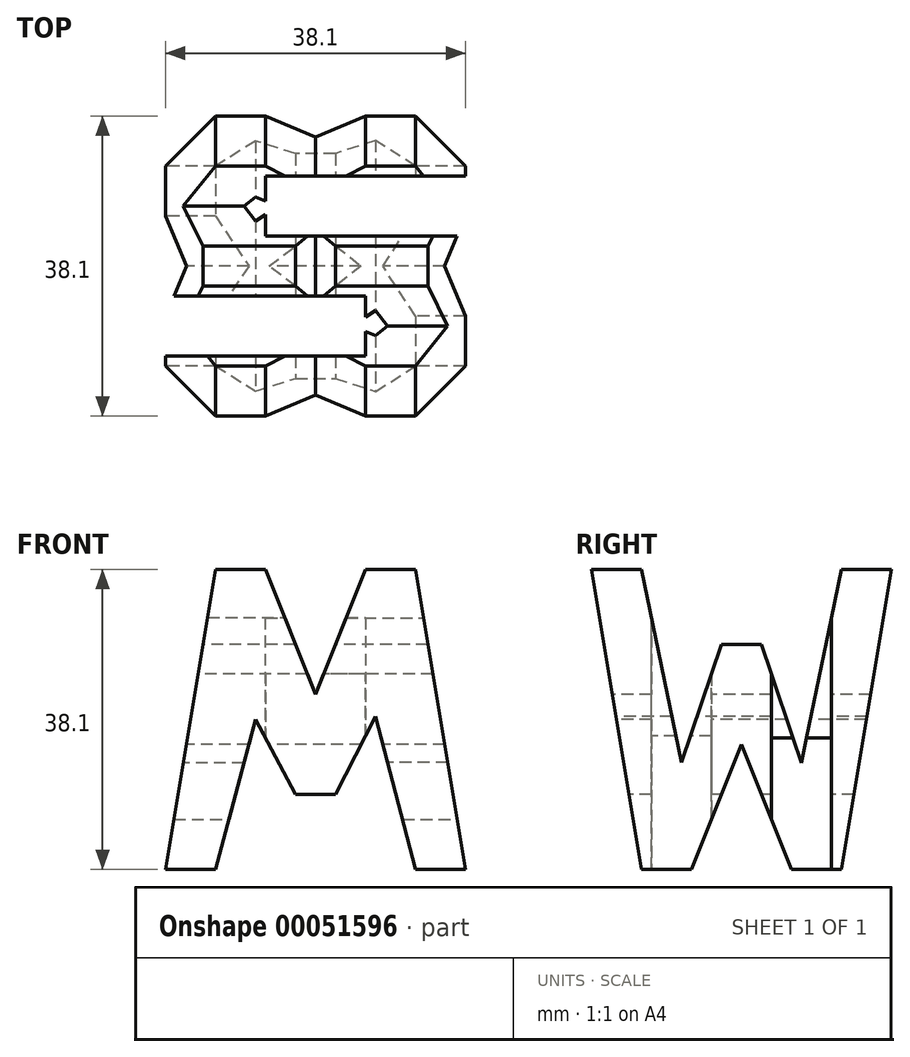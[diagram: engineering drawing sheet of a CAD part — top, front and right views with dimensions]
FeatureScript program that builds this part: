
annotation { "Feature Type Name" : "Feature", "Feature Type Description" : "" }
export const myFeature = defineFeature(function(context is Context, id is Id, definition is map)
    precondition{}
    {
        {
            var Q0;
            Q0=qCreatedBy(makeId("Front.planeOp"),FACE);
            var sketch = newSketch(context, id + "F0", { "sketchPlane" : qUnion([Q0])});
            skLineSegment(sketch, "E0", {"start": v(0, 0) * mm, "end": v(-38.1, 0) * mm});
            skLineSegment(sketch, "E1", {"start": v(-38.1, 0) * mm, "end": v(-38.1, 38.1) * mm});
            skLineSegment(sketch, "E2", {"start": v(-38.1, 38.1) * mm, "end": v(0, 38.1) * mm});
            skLineSegment(sketch, "E3", {"start": v(0, 38.1) * mm, "end": v(0, 0) * mm});
            skSolve(sketch);
        }
        {
            var Q0;
            Q0=makeQuery(id+"F0.imprint","IMPRINT",FACE,{"disambiguationData":[TD([[makeQuery(id+"F0.imprint","IMPRINT",EDGE,{"derivedFrom":sQuery(id+"F0.wireOp",EDGE,"E0")}),-1.0]])]});
            extrude(context, id + "F1", {"entities" : qUnion([Q0]), "depth" : 38.1 * mm});
        }
        {
            var Q0;
            Q0=qCreatedBy(makeId("Front.planeOp"),FACE);
            cPlane(context, id + "F2", {"entities" : qUnion([Q0]), "cplaneType" : CPlaneType.OFFSET, "offset" : 38.1 * mm, "width" : 152.4 * mm, "height" : 152.4 * mm});
        }
        {
            var Q0;
            Q0=qCreatedBy(makeId("Right.planeOp"),FACE);
            cPlane(context, id + "F3", {"entities" : qUnion([Q0]), "cplaneType" : CPlaneType.OFFSET, "offset" : 38.1 * mm, "oppositeDirection" : true, "width" : 152.4 * mm, "height" : 152.4 * mm});
        }
        {
            var Q0;
            Q0=qCreatedBy(makeId("Top.planeOp"),FACE);
            cPlane(context, id + "F4", {"entities" : qUnion([Q0]), "cplaneType" : CPlaneType.OFFSET, "offset" : 38.1 * mm, "width" : 152.4 * mm, "height" : 152.4 * mm});
        }
        {
            var Q0;
            Q0=qCreatedBy(id+"F3.planeOp",FACE);
            var sketch = newSketch(context, id + "F5", { "sketchPlane" : qUnion([Q0])});
            skLineSegment(sketch, "E4", {"start": v(0, 0) * mm, "end": v(0, 38.1) * mm});
            skLineSegment(sketch, "E5", {"start": v(0, 38.1) * mm, "end": v(-38.1, 38.1) * mm});
            skLineSegment(sketch, "E6", {"start": v(-38.1, 38.1) * mm, "end": v(-38.1, 0) * mm});
            skLineSegment(sketch, "E7", {"start": v(-38.1, 0) * mm, "end": v(0, 0) * mm});
            skLineSegment(sketch, "E8", {"start": v(-38.1, 38.1) * mm, "end": v(-31.75, 0) * mm});
            skLineSegment(sketch, "E9", {"start": v(-31.75, 0) * mm, "end": v(-25.4, 0) * mm});
            skLineSegment(sketch, "E10", {"start": v(-25.4, 0) * mm, "end": v(-19.05, 15.87) * mm});
            skLineSegment(sketch, "E11", {"start": v(-19.05, 15.87) * mm, "end": v(-12.7, 0) * mm});
            skLineSegment(sketch, "E12", {"start": v(-12.7, 0) * mm, "end": v(-6.35, 0) * mm});
            skLineSegment(sketch, "E13", {"start": v(-6.35, 0) * mm, "end": v(0, 38.1) * mm});
            skLineSegment(sketch, "E14", {"start": v(-6.35, 38.1) * mm, "end": v(-11.43, 13.5) * mm});
            skLineSegment(sketch, "E15", {"start": v(-11.43, 13.5) * mm, "end": v(-16.5, 28.57) * mm});
            skLineSegment(sketch, "E16", {"start": v(-16.5, 28.57) * mm, "end": v(-21.59, 28.57) * mm});
            skLineSegment(sketch, "E17", {"start": v(-21.59, 28.57) * mm, "end": v(-26.67, 13.62) * mm});
            skLineSegment(sketch, "E18", {"start": v(-26.67, 13.62) * mm, "end": v(-31.75, 38.1) * mm});
            skSolve(sketch);
        }
        {
            var Q0;
            {var subQ0=sQuery(id+"F5.wireOp",EDGE,"E14");Q0=makeQuery(id+"F5.imprint","IMPRINT",FACE,{"disambiguationData":[TD([[makeQuery(id+"F5.imprint","IMPRINT",EDGE,{"derivedFrom":subQ0}),-1.0]])]});}
            var Q1;
            {var subQ0=sQuery(id+"F5.wireOp",EDGE,"E10");Q1=makeQuery(id+"F5.imprint","IMPRINT",FACE,{"disambiguationData":[TD([[makeQuery(id+"F5.imprint","IMPRINT",EDGE,{"derivedFrom":subQ0}),-1.0]])]});}
            var Q2;
            {var subQ0=sQuery(id+"F5.wireOp",EDGE,"E4");Q2=makeQuery(id+"F5.imprint","IMPRINT",FACE,{"disambiguationData":[TD([[makeQuery(id+"F5.imprint","IMPRINT",EDGE,{"derivedFrom":subQ0}),1.0]])]});}
            var Q3;
            {var subQ0=sQuery(id+"F5.wireOp",EDGE,"E6");Q3=makeQuery(id+"F5.imprint","IMPRINT",FACE,{"disambiguationData":[TD([[makeQuery(id+"F5.imprint","IMPRINT",EDGE,{"derivedFrom":subQ0}),1.0]])]});}
            extrude(context, id + "F6", {"entities" : qUnion([Q0, Q1, Q2, Q3]), "operationType" : NewBodyOperationType.REMOVE, "depth" : 38.1 * mm});
        }
        {
            var Q0;
            Q0=qCreatedBy(id+"F2.planeOp",FACE);
            var sketch = newSketch(context, id + "F7", { "sketchPlane" : qUnion([Q0])});
            skLineSegment(sketch, "E19", {"start": v(0, 0) * mm, "end": v(0, 38.1) * mm});
            skLineSegment(sketch, "E20", {"start": v(0, 38.1) * mm, "end": v(-38.1, 38.1) * mm});
            skLineSegment(sketch, "E21", {"start": v(-38.1, 38.1) * mm, "end": v(-38.1, 0) * mm});
            skLineSegment(sketch, "E22", {"start": v(-38.1, 0) * mm, "end": v(0, 0) * mm});
            skLineSegment(sketch, "E23", {"start": v(-38.1, 0) * mm, "end": v(-31.75, 38.1) * mm});
            skLineSegment(sketch, "E24", {"start": v(-31.75, 38.1) * mm, "end": v(-25.4, 38.1) * mm});
            skLineSegment(sketch, "E25", {"start": v(-25.4, 38.1) * mm, "end": v(-19.05, 22.23) * mm});
            skLineSegment(sketch, "E26", {"start": v(-19.05, 22.23) * mm, "end": v(-12.7, 38.1) * mm});
            skLineSegment(sketch, "E27", {"start": v(-12.7, 38.1) * mm, "end": v(-6.35, 38.1) * mm});
            skLineSegment(sketch, "E28", {"start": v(-6.35, 38.1) * mm, "end": v(0, 0) * mm});
            skLineSegment(sketch, "E29", {"start": v(-6.35, 0) * mm, "end": v(-11.43, 19.46) * mm});
            skLineSegment(sketch, "E30", {"start": v(-11.43, 19.46) * mm, "end": v(-16.5, 9.53) * mm});
            skLineSegment(sketch, "E31", {"start": v(-16.5, 9.53) * mm, "end": v(-21.59, 9.53) * mm});
            skLineSegment(sketch, "E32", {"start": v(-21.59, 9.53) * mm, "end": v(-26.67, 19.09) * mm});
            skLineSegment(sketch, "E33", {"start": v(-26.67, 19.09) * mm, "end": v(-31.75, 0) * mm});
            skLineSegment(sketch, "E34", {"start": v(-31.75, 0) * mm, "end": v(-38.1, 0) * mm});
            skSolve(sketch);
        }
        {
            var Q0;
            {var subQ0=sQuery(id+"F7.wireOp",EDGE,"E29");Q0=makeQuery(id+"F7.imprint","IMPRINT",FACE,{"disambiguationData":[TD([[makeQuery(id+"F7.imprint","IMPRINT",EDGE,{"derivedFrom":subQ0}),1.0]])]});}
            var Q1;
            {var subQ0=sQuery(id+"F7.wireOp",EDGE,"E19");Q1=makeQuery(id+"F7.imprint","IMPRINT",FACE,{"disambiguationData":[TD([[makeQuery(id+"F7.imprint","IMPRINT",EDGE,{"derivedFrom":subQ0}),1.0]])]});}
            var Q2;
            {var subQ0=sQuery(id+"F7.wireOp",EDGE,"E25");Q2=makeQuery(id+"F7.imprint","IMPRINT",FACE,{"disambiguationData":[TD([[makeQuery(id+"F7.imprint","IMPRINT",EDGE,{"derivedFrom":subQ0}),1.0]])]});}
            var Q3;
            {var subQ0=sQuery(id+"F7.wireOp",EDGE,"E21");Q3=makeQuery(id+"F7.imprint","IMPRINT",FACE,{"disambiguationData":[TD([[makeQuery(id+"F7.imprint","IMPRINT",EDGE,{"derivedFrom":subQ0}),1.0]])]});}
            extrude(context, id + "F8", {"entities" : qUnion([Q0, Q1, Q2, Q3]), "operationType" : NewBodyOperationType.REMOVE, "oppositeDirection" : true, "depth" : 38.1 * mm});
        }
        {
            var Q0;
            Q0=qCreatedBy(id+"F4.planeOp",FACE);
            var sketch = newSketch(context, id + "F9", { "sketchPlane" : qUnion([Q0])});
            skLineSegment(sketch, "E35", {"start": v(0, 0) * mm, "end": v(-38.1, 0) * mm});
            skLineSegment(sketch, "E36", {"start": v(-38.1, 0) * mm, "end": v(-38.1, -38.1) * mm});
            skLineSegment(sketch, "E37", {"start": v(-38.1, -38.1) * mm, "end": v(0, -38.1) * mm});
            skLineSegment(sketch, "E38", {"start": v(0, -38.1) * mm, "end": v(0, 0) * mm});
            skLineSegment(sketch, "E39", {"start": v(0, 0) * mm, "end": v(0, -7.62) * mm});
            skLineSegment(sketch, "E40", {"start": v(0, -7.62) * mm, "end": v(-25.4, -7.62) * mm});
            skLineSegment(sketch, "E41", {"start": v(-25.4, -7.62) * mm, "end": v(-25.4, -15.24) * mm});
            skLineSegment(sketch, "E42", {"start": v(-25.4, -15.24) * mm, "end": v(0, -15.24) * mm});
            skLineSegment(sketch, "E43", {"start": v(-38.1, -22.86) * mm, "end": v(-12.7, -22.86) * mm});
            skLineSegment(sketch, "E44", {"start": v(-12.7, -22.86) * mm, "end": v(-12.7, -30.48) * mm});
            skLineSegment(sketch, "E45", {"start": v(-12.7, -30.48) * mm, "end": v(-38.1, -30.48) * mm});
            skSolve(sketch);
        }
        {
            var Q0;
            {var subQ0=sQuery(id+"F9.wireOp",EDGE,"E40");Q0=makeQuery(id+"F9.imprint","IMPRINT",FACE,{"disambiguationData":[TD([[makeQuery(id+"F9.imprint","IMPRINT",EDGE,{"derivedFrom":subQ0}),1.0]])]});}
            var Q1;
            {var subQ0=sQuery(id+"F9.wireOp",EDGE,"E43");Q1=makeQuery(id+"F9.imprint","IMPRINT",FACE,{"disambiguationData":[TD([[makeQuery(id+"F9.imprint","IMPRINT",EDGE,{"derivedFrom":subQ0}),-1.0]])]});}
            extrude(context, id + "F10", {"entities" : qUnion([Q0, Q1]), "operationType" : NewBodyOperationType.REMOVE, "oppositeDirection" : true, "depth" : 38.1 * mm});
        }
    });
